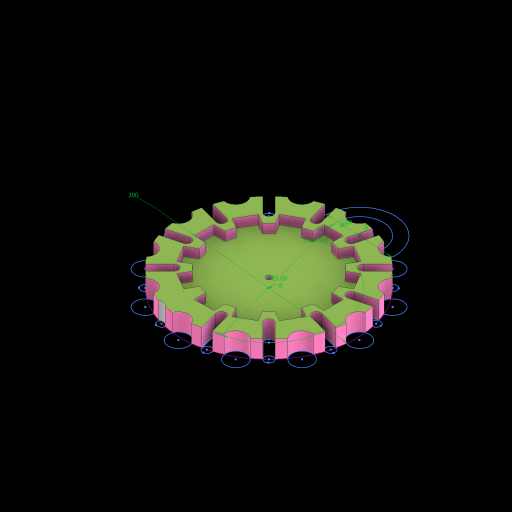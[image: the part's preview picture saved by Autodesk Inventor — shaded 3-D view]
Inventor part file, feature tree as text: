
AUTODESK INVENTOR PART (.ipt)
format: ipt  version: 2023 (Build 270158000, 158)  size: 419,840 bytes
history: native  units: mm
features: sketch x4, extrude x4
ambient origin geometry x8: Origin, YZ Plane, XZ Plane, XY Plane, X Axis, Y Axis, Z Axis, Center Point
bodies: Solid1 (feature_tree)
feature tree (8):
  sketch  "Sketch1"  dims[d1=80.0mm d2=100.0mm d3=22.5deg d4=20.712mm d5=50.0mm d6=54.123064mm d7=10.0mm d8=25.858174mm d9=65.0mm d10=360.0deg d11=7.0mm d12=7.0mm d13=15.0mm d14=15.0mm d15=10.0mm d16=200.0mm]
  sketch  "Sketch2"  dims[d17=15.0deg d19=90.0deg]
  extrude  "Extrusion1"  Depth=10.0mm
  extrude  "Extrusion2"  TaperAngle=90.0deg  [1 undecoded]
  extrude  "Extrusion3"  Depth=10.0mm
  extrude  "Extrusion4"  Depth=20.0mm TaperAngle=360.0deg
  sketch  "Sketch3"  dims[d20=10.0mm d21=10.0mm]
  sketch  "Sketch4"  dims[d22=80.0mm d23=120.0mm d25=360.0deg d27=6.0mm d28=5.0mm d29=20.0mm d30=0.0mm d34=120.0mm d36=360.0deg d38=10.0mm d39=0.0mm d40=20.0mm d41=0.0mm d42=20.0mm d43=0.0mm]
note: 1 required parameter value undecoded (feature->parameter linkage not recoverable at this tier; creation-order binding heuristic only, values carry confidence <= 0.55)
